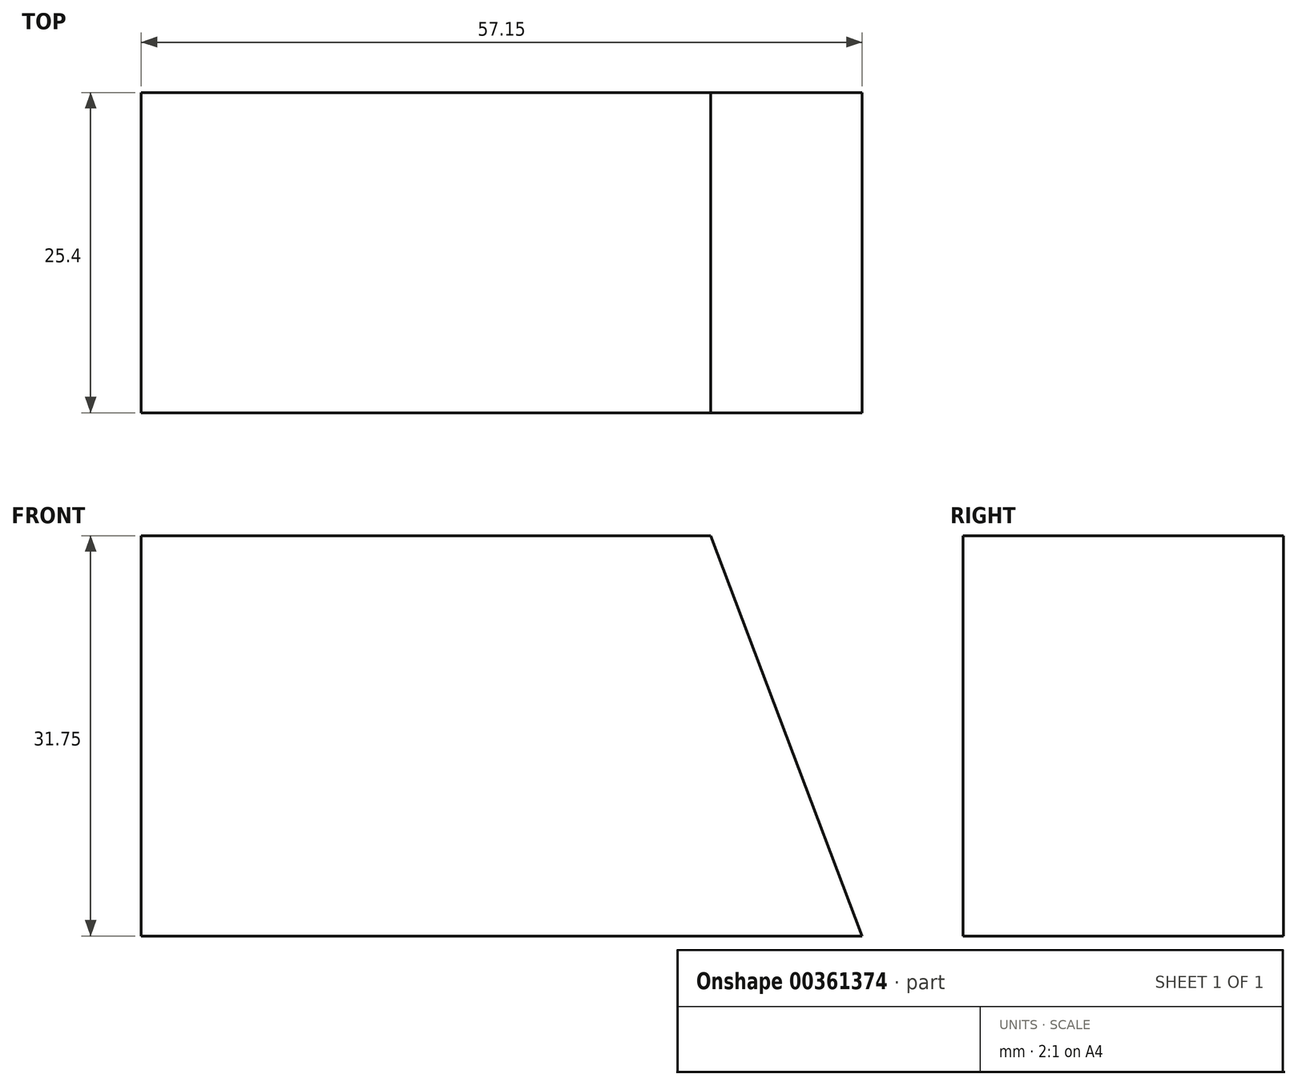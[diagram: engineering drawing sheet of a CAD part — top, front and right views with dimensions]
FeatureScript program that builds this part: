
annotation { "Feature Type Name" : "Feature", "Feature Type Description" : "" }
export const myFeature = defineFeature(function(context is Context, id is Id, definition is map)
    precondition{}
    {
        {
            var Q0;
            Q0=qCreatedBy(makeId("Front.planeOp"),FACE);
            var sketch = newSketch(context, id + "F0", { "sketchPlane" : qUnion([Q0])});
            skLineSegment(sketch, "E0", {"start": v(6.77, 0) * mm, "end": v(6.77, 31.75) * mm});
            skLineSegment(sketch, "E1", {"start": v(6.77, 31.75) * mm, "end": v(63.92, 31.75) * mm});
            skLineSegment(sketch, "E2", {"start": v(63.92, 31.75) * mm, "end": v(63.92, 0) * mm});
            skLineSegment(sketch, "E3", {"start": v(63.92, 0) * mm, "end": v(6.77, 0) * mm});
            skSolve(sketch);
        }
        {
            var Q0;
            Q0 = qSketchRegion(id + "F0", true);
            extrude(context, id + "F1", {"entities" : qUnion([Q0]), "depth" : 25.4 * mm});
        }
        {
            var Q0;
            Q0=makeQuery(id+"F1.opExtrude","CAP_FACE",FACE,{"disambiguationData":[OSD([sQuery(id+"F0.wireOp",EDGE,"E0"),sQuery(id+"F0.wireOp",EDGE,"E1"),sQuery(id+"F0.wireOp",EDGE,"E2"),sQuery(id+"F0.wireOp",EDGE,"E3")])],"isStart":false});
            var sketch = newSketch(context, id + "F2", { "sketchPlane" : qUnion([Q0])});
            skLineSegment(sketch, "E4", {"start": v(63.92, 0) * mm, "end": v(51.9, 31.75) * mm});
            skSolve(sketch);
        }
        {
            var Q0;
            {var subQ0=sQuery(id+"F2.wireOp",EDGE,"E4");Q0=makeQuery(id+"F2.imprint","IMPRINT",FACE,{"disambiguationData":[TD([[makeQuery(id+"F2.imprint","IMPRINT",EDGE,{"derivedFrom":subQ0}),-1.0]])]});}
            extrude(context, id + "F3", {"entities" : qUnion([Q0]), "operationType" : NewBodyOperationType.REMOVE, "oppositeDirection" : true, "depth" : 38.1 * mm});
        }
    });
